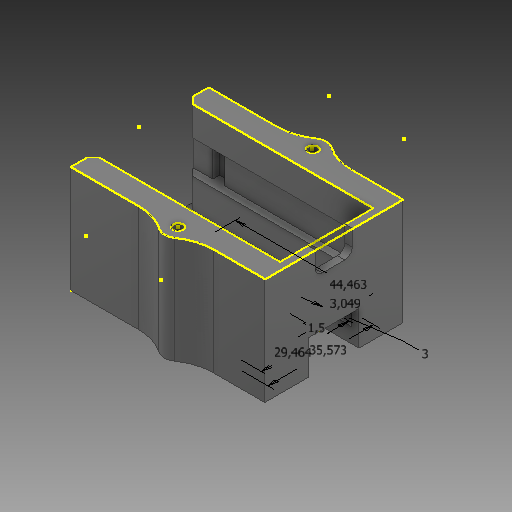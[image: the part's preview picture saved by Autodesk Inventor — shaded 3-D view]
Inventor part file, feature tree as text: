
AUTODESK INVENTOR PART (.ipt)
format: ipt  version: 2020 (Build 240168000, 168)  size: 301,568 bytes
history: native  units: mm
features: sketch x6, extrude x4, projected_geometry x3, hole x2, other x1, fillet x1, imported_body x1
ambient origin geometry x8: Origin, YZ Plane, XZ Plane, XY Plane, X Axis, Y Axis, Z Axis, Center Point
bodies: Body1 (feature_tree)
feature tree (18):
  other  "Твердое тело1"
  sketch  "Эскиз1"
  extrude  "Выдавливание1"  Depth=8.0mm
  fillet  "Сопряжение1"  Radius=12.5mm
  extrude  "Выдавливание2"  TaperAngle=0.0deg  [1 undecoded]
  extrude  "Выдавливание3"  Depth=2.5mm
  sketch  "Эскиз6"
  hole  "Отверстие1"  [1 undecoded]
  hole  "Отверстие2"  [1 undecoded]
  extrude  "Выдавливание4"  Depth=35.5mm
  sketch  "Эскиз7"
  projected_geometry  "Спроецированная петля1"
  sketch  "Эскиз2"
  sketch  "Эскиз3"
  projected_geometry  "Спроецированная петля2"
  sketch  "Эскиз4"
  projected_geometry  "Спроецированная петля3"
  imported_body  "БазТело1"
note: 3 required parameter values undecoded (feature->parameter linkage not recoverable at this tier; creation-order binding heuristic only, values carry confidence <= 0.55)
